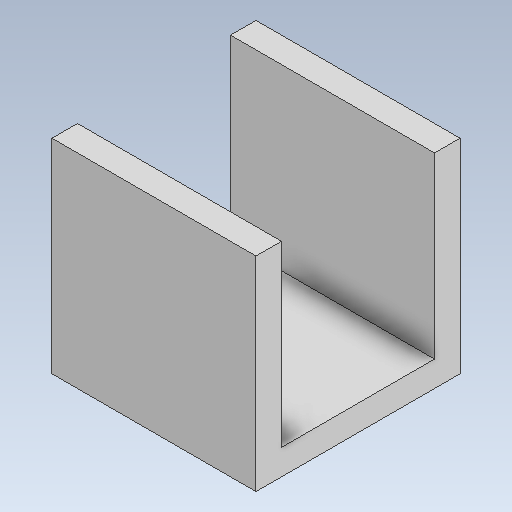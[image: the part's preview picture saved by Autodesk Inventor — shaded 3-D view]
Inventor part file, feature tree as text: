
AUTODESK INVENTOR PART (.ipt)
format: ipt  version: 2021 (Build 250183000, 183)  size: 97,792 bytes
history: native  units: in
note: dims shown in document units (in); Inventor stores cm internally (conversion verified against a paired STEP export)
features: other x3, sketch x1
ambient origin geometry x8: Origin, YZ Plane, XZ Plane, XY Plane, X Axis, Y Axis, Z Axis, Center Point
bodies: Solid1 (feature_tree)
feature tree (4):
  other  "halfinchCChannel.ipt"
  other  "Solid1::halfinchCChannel.ipt"
  other  "TaggingFeature1"
  sketch  "Sketch2"  dims[d0=0.3937in]
